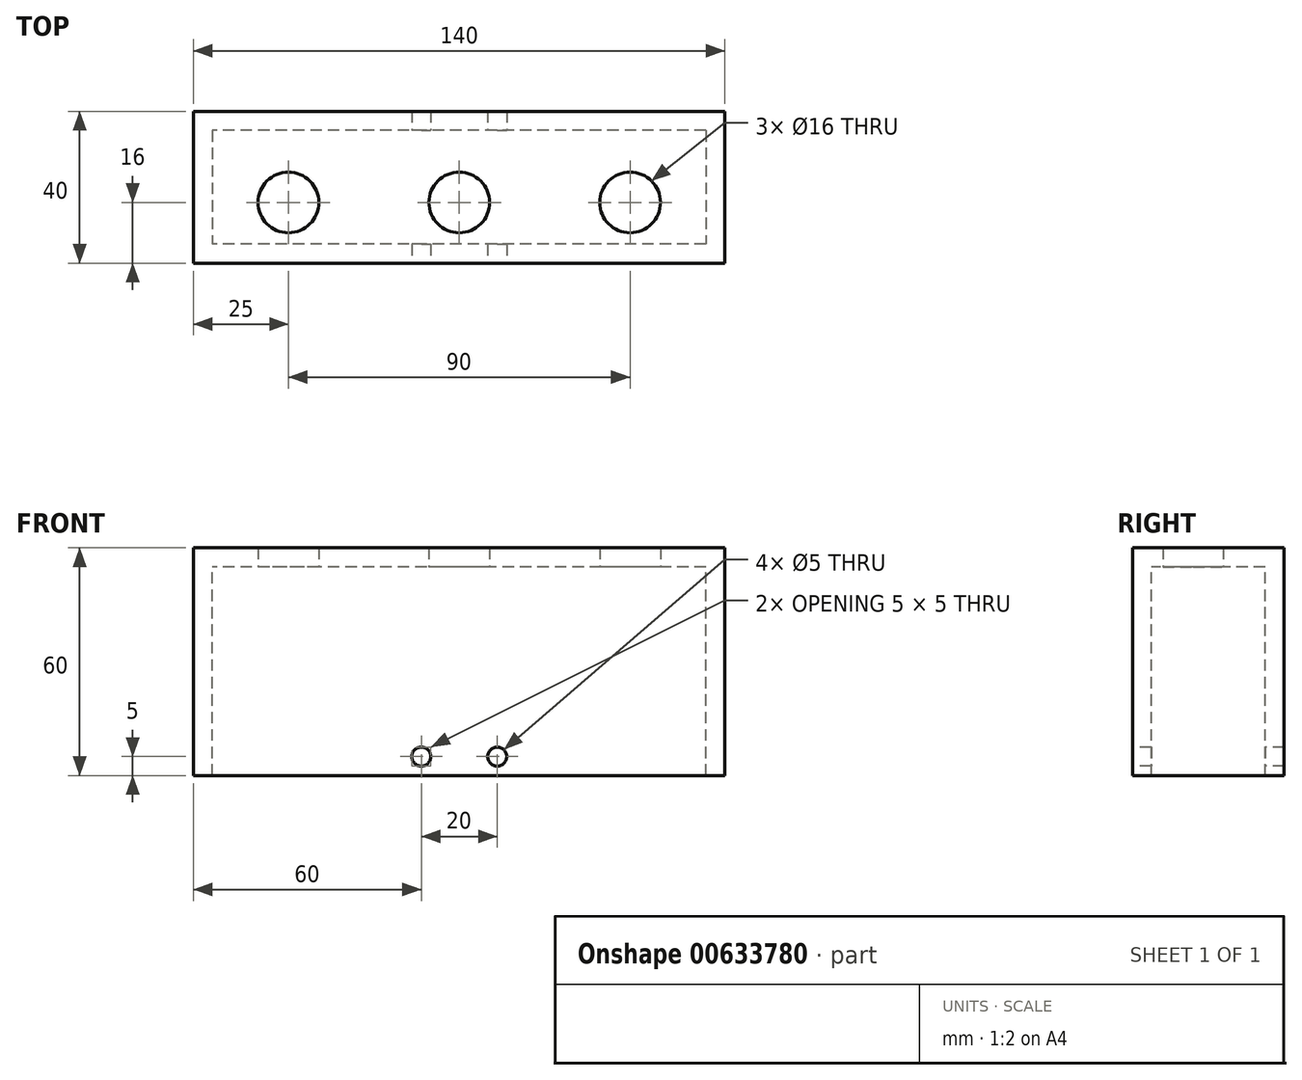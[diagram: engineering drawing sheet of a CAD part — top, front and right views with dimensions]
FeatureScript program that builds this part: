
annotation { "Feature Type Name" : "Feature", "Feature Type Description" : "" }
export const myFeature = defineFeature(function(context is Context, id is Id, definition is map)
    precondition{}
    {
        {
            var Q0;
            Q0=qCreatedBy(makeId("Top.planeOp"),FACE);
            var sketch = newSketch(context, id + "F0", { "sketchPlane" : qUnion([Q0])});
            skLineSegment(sketch, "E0.bottom", {"start": v(70, 20) * mm, "end": v(-70, 20) * mm});
            skLineSegment(sketch, "E0.top", {"start": v(70, -20) * mm, "end": v(-70, -20) * mm});
            skLineSegment(sketch, "E0.left", {"start": v(70, 20) * mm, "end": v(70, -20) * mm});
            skLineSegment(sketch, "E0.right", {"start": v(-70, 20) * mm, "end": v(-70, -20) * mm});
            skPoint(sketch, "E0.middle", {"position": v(0, 0) * mm});
            skCircle(sketch, "E1", {"center": v(0, -4) * mm, "radius": 8 * mm});
            skCircle(sketch, "E2", {"center": v(-45, -4) * mm, "radius": 8 * mm});
            skCircle(sketch, "E3.MirrorC", {"center": v(45, -4) * mm, "radius": 8 * mm});
            skSolve(sketch);
        }
        {
            var Q0;
            Q0=makeQuery(id+"F0.imprint","IMPRINT",FACE,{"disambiguationData":[TD([[makeQuery(id+"F0.imprint","IMPRINT",EDGE,{"derivedFrom":sQuery(id+"F0.wireOp",EDGE,"E0.bottom")}),1.0]])]});
            extrude(context, id + "F1", {"entities" : qUnion([Q0]), "depth" : 5 * mm, "offsetDistance" : 25 * mm});
        }
        {
            var Q0;
            Q0=makeQuery(id+"F1.opExtrude","CAP_FACE",FACE,{"disambiguationData":[OSD([sQuery(id+"F0.wireOp",EDGE,"E0.bottom"),sQuery(id+"F0.wireOp",EDGE,"E0.top"),sQuery(id+"F0.wireOp",EDGE,"E0.left"),sQuery(id+"F0.wireOp",EDGE,"E0.right"),sQuery(id+"F0.wireOp",EDGE,"E1"),sQuery(id+"F0.wireOp",EDGE,"E2"),sQuery(id+"F0.wireOp",EDGE,"E3.MirrorC")])],"isStart":true});
            var sketch = newSketch(context, id + "F2", { "sketchPlane" : qUnion([Q0])});
            skLineSegment(sketch, "E4.bottom", {"start": v(70, 20) * mm, "end": v(-70, 20) * mm});
            skLineSegment(sketch, "E4.top", {"start": v(70, 15) * mm, "end": v(-70, 15) * mm});
            skLineSegment(sketch, "E4.left", {"start": v(70, 20) * mm, "end": v(70, 15) * mm});
            skLineSegment(sketch, "E4.right", {"start": v(-70, 20) * mm, "end": v(-70, 15) * mm});
            skPoint(sketch, "E4.middle", {"position": v(0, 17.5) * mm});
            skLineSegment(sketch, "E5.MirrorCS", {"start": v(70, -15) * mm, "end": v(-70, -15) * mm});
            skLineSegment(sketch, "E6.MirrorCS", {"start": v(70, -20) * mm, "end": v(-70, -20) * mm});
            skLineSegment(sketch, "E7.MirrorCS", {"start": v(70, -20) * mm, "end": v(70, -15) * mm});
            skLineSegment(sketch, "E8.MirrorCS", {"start": v(-70, -20) * mm, "end": v(-70, -15) * mm});
            skSolve(sketch);
        }
        {
            var Q0;
            Q0 = qSketchRegion(id + "F2", true);
            extrude(context, id + "F3", {"entities" : qUnion([Q0]), "operationType" : NewBodyOperationType.ADD, "depth" : 55 * mm, "offsetDistance" : 25 * mm});
        }
        {
            var Q0;
            Q0=makeQuery(id+"F1.opExtrude","CAP_FACE",FACE,{"disambiguationData":[OSD([sQuery(id+"F0.wireOp",EDGE,"E0.bottom"),sQuery(id+"F0.wireOp",EDGE,"E0.top"),sQuery(id+"F0.wireOp",EDGE,"E0.left"),sQuery(id+"F0.wireOp",EDGE,"E0.right"),sQuery(id+"F0.wireOp",EDGE,"E1"),sQuery(id+"F0.wireOp",EDGE,"E2"),sQuery(id+"F0.wireOp",EDGE,"E3.MirrorC")])],"isStart":true});
            var sketch = newSketch(context, id + "F4", { "sketchPlane" : qUnion([Q0])});
            skLineSegment(sketch, "E9.bottom", {"start": v(-70, -15) * mm, "end": v(-65, -15) * mm});
            skLineSegment(sketch, "E9.top", {"start": v(-70, 15) * mm, "end": v(-65, 15) * mm});
            skLineSegment(sketch, "E9.left", {"start": v(-70, -15) * mm, "end": v(-70, 15) * mm});
            skLineSegment(sketch, "E9.right", {"start": v(-65, -15) * mm, "end": v(-65, 15) * mm});
            skPoint(sketch, "E9.middle", {"position": v(-67.5, 0) * mm});
            skLineSegment(sketch, "E10.MirrorCS", {"start": v(65, -15) * mm, "end": v(65, 15) * mm});
            skLineSegment(sketch, "E11.MirrorCS", {"start": v(70, -15) * mm, "end": v(70, 15) * mm});
            skLineSegment(sketch, "E12.MirrorCS", {"start": v(70, 15) * mm, "end": v(65, 15) * mm});
            skLineSegment(sketch, "E13.MirrorCS", {"start": v(70, -15) * mm, "end": v(65, -15) * mm});
            skSolve(sketch);
        }
        {
            var Q0;
            Q0 = qSketchRegion(id + "F4", true);
            extrude(context, id + "F5", {"entities" : qUnion([Q0]), "operationType" : NewBodyOperationType.ADD, "depth" : 55 * mm, "offsetDistance" : 25 * mm});
        }
        {
            var Q0;
            Q0=makeQuery(id+"F3.boolean.opBoolean","MERGE",FACE,{"derivedFrom":[makeQuery(id+"F1.opExtrude","SWEPT_FACE",FACE,{"disambiguationData":[OSD([sQuery(id+"F0.wireOp",EDGE,"E0.top")])]}),makeQuery(id+"F3.opExtrude","SWEPT_FACE",FACE,{"disambiguationData":[OSD([sQuery(id+"F2.wireOp",EDGE,"E4.bottom")])]})]});
            var sketch = newSketch(context, id + "F6", { "sketchPlane" : qUnion([Q0])});
            skCircle(sketch, "E14", {"center": v(10, -50) * mm, "radius": 2.5 * mm});
            skCircle(sketch, "E15", {"center": v(-10, -50) * mm, "radius": 2.5 * mm});
            skSolve(sketch);
        }
        {
            var Q0;
            Q0 = qSketchRegion(id + "F6", true);
            extrude(context, id + "F7", {"entities" : qUnion([Q0]), "operationType" : NewBodyOperationType.REMOVE, "oppositeDirection" : true, "depth" : 60 * mm, "offsetDistance" : 25 * mm});
        }
    });
